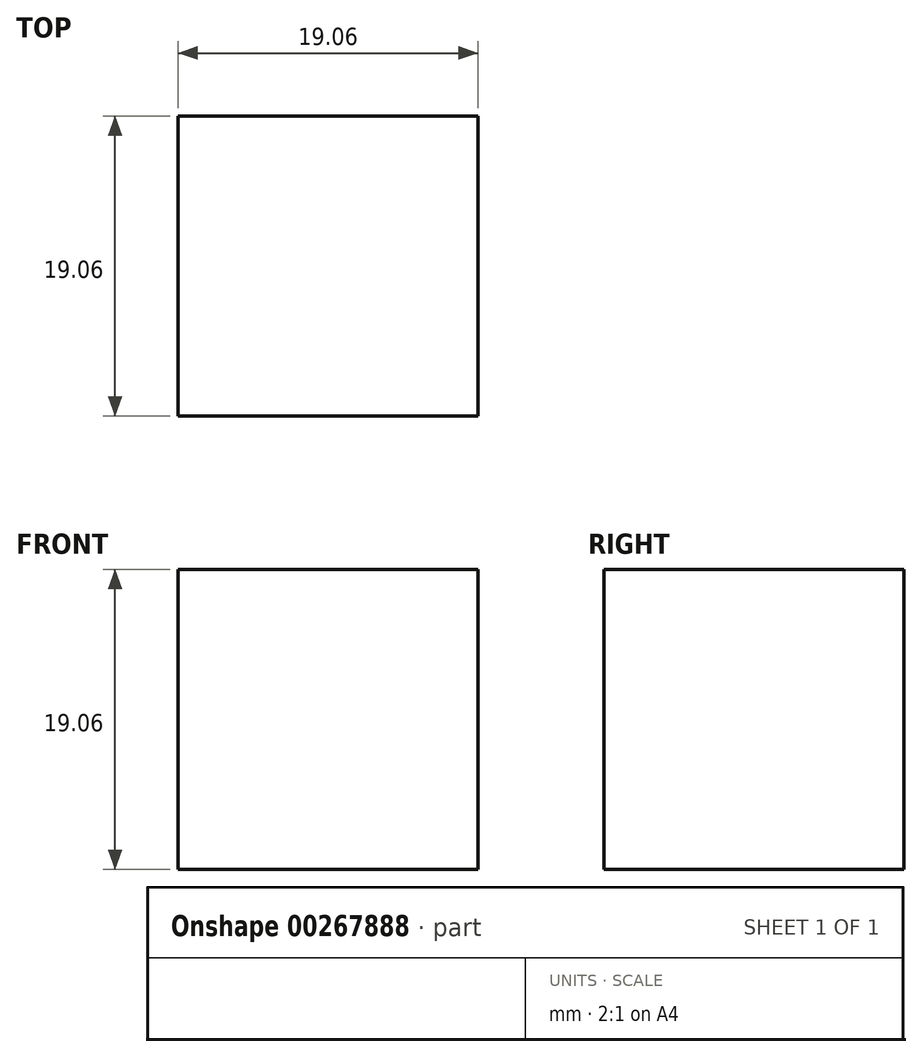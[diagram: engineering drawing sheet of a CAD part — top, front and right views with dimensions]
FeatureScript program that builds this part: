
annotation { "Feature Type Name" : "Feature", "Feature Type Description" : "" }
export const myFeature = defineFeature(function(context is Context, id is Id, definition is map)
    precondition{}
    {
        {
            var Q0;
            Q0=qCreatedBy(makeId("Front.planeOp"),FACE);
            var sketch = newSketch(context, id + "F0", { "sketchPlane" : qUnion([Q0])});
            skLineSegment(sketch, "E0.bottom", {"start": v(-9.53, 9.53) * mm, "end": v(9.53, 9.53) * mm});
            skLineSegment(sketch, "E0.top", {"start": v(-9.53, -9.52) * mm, "end": v(9.52, -9.52) * mm});
            skLineSegment(sketch, "E0.left", {"start": v(-9.53, 9.53) * mm, "end": v(-9.53, -9.52) * mm});
            skLineSegment(sketch, "E0.right", {"start": v(9.53, 9.53) * mm, "end": v(9.52, -9.52) * mm});
            skPoint(sketch, "E0.middle", {"position": v(0, 0) * mm});
            skSolve(sketch);
        }
        {
            var Q0;
            Q0 = qSketchRegion(id + "F0", true);
            extrude(context, id + "F1", {"entities" : qUnion([Q0]), "endBound" : BoundingType.SYMMETRIC, "depth" : 19.05 * mm});
        }
    });
